# Revit family: equip-water-cooler-elkay-vrc8v2-ezh2o
name_source: partatom
category: Plumbing Fixtures
units: mm (PartAtom-declared; Revit-internal decimal feet)

## family parameters
Always vertical = Yes
Cut with Voids When Loaded = No
OmniClass Number = 23.45.00.00
OmniClass Title = Sanitary, Laundry, and Cleaning Equipment
Part Type = Normal
Room Calculation Point = No
Round Connector Dimension = Use Radius
Shared = No
Work Plane-Based = No

## types (2) — shared parameters
Activation = -
Apparent Load Phase 1 = 0 VA
Basin Material = Metal - Steel - Stainless - Chrome
Bubbler = -
Button Material = Plastic - Brown
CW Connection = Yes
Cooler Bottom = 1' - 0 3/8"
Cooler Depth = 1' - 6 5/8"
Cooler Height = 1' - 8 5/8"
Cooler Rear Panel Depth = 0' - 6 27/32"
Cooler Width = 1' - 6 1/16"
Description = Mechanical pushbar actuated water cooler
Dispenser Depth = 0' - 8"
Dispenser Height = 2' - 3 1/16"
Filter = -
Glass Filter = -
HW Connection = No
Manufacturer = Elkay Manufacturing
Numbe of Poles = 1
Orifice Height = 2' - 9"
Orifice to Rim = 0' - 1 13/16"
Panel Material = Metal - Steel - Stainless - Color 1
Power Factor = 1
Product ID = -
Refrigerated = -
Rim Height = 2' - 7 3/16"
Rim to Dispenser = 0' - 4 1/8"
Sanitary Service Radius = 0' - 0 5/8"
Specification URL = http://www.elkayusa.com
Type = Single
URL = http://www.Elkayusa.com
Vent Connection = No
Version = 1.0.0.0
Voltage = 0 V
Volts/Hertz = -
Waste Connection = Yes
Water Service Flow = 0 GPM
Water Service Size Radius = 0' - 0 1/4"

## type names (no varying parameters)
- VRCGRN8WSK
- LVRCGRN8WSK

note: column(s) folded — value = type name in every type: Model

## geometry (parser evidence)
native form markers: Sweep x3
no freeform markers — native parametric forms only
